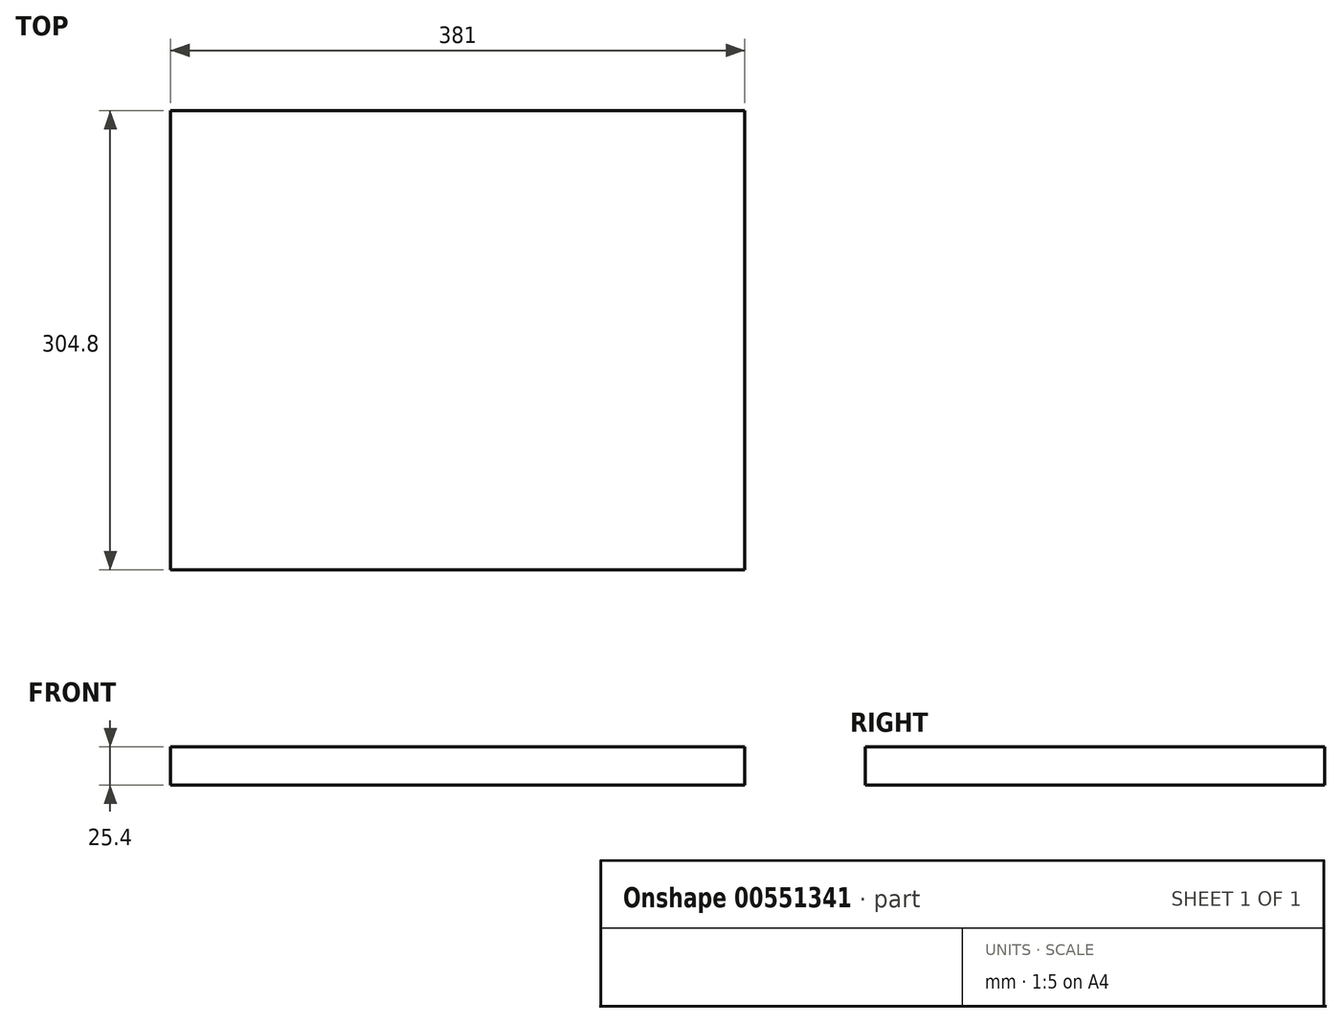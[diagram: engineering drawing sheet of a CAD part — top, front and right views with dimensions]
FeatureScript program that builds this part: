
annotation { "Feature Type Name" : "Feature", "Feature Type Description" : "" }
export const myFeature = defineFeature(function(context is Context, id is Id, definition is map)
    precondition{}
    {
        {
            var Q0;
            Q0=qCreatedBy(makeId("Top.planeOp"),FACE);
            var sketch = newSketch(context, id + "F0", { "sketchPlane" : qUnion([Q0])});
            skLineSegment(sketch, "E0.bottom", {"start": v(-268.3, 160.75) * mm, "end": v(112.7, 160.75) * mm});
            skLineSegment(sketch, "E0.top", {"start": v(-268.3, -144.05) * mm, "end": v(112.7, -144.05) * mm});
            skLineSegment(sketch, "E0.left", {"start": v(-268.3, 160.75) * mm, "end": v(-268.3, -144.05) * mm});
            skLineSegment(sketch, "E0.right", {"start": v(112.7, 160.75) * mm, "end": v(112.7, -144.05) * mm});
            skSolve(sketch);
        }
        {
            var Q0;
            Q0 = qSketchRegion(id + "F0", true);
            extrude(context, id + "F1", {"entities" : qUnion([Q0]), "depth" : 25.4 * mm, "offsetDistance" : 25.4 * mm});
        }
    });
